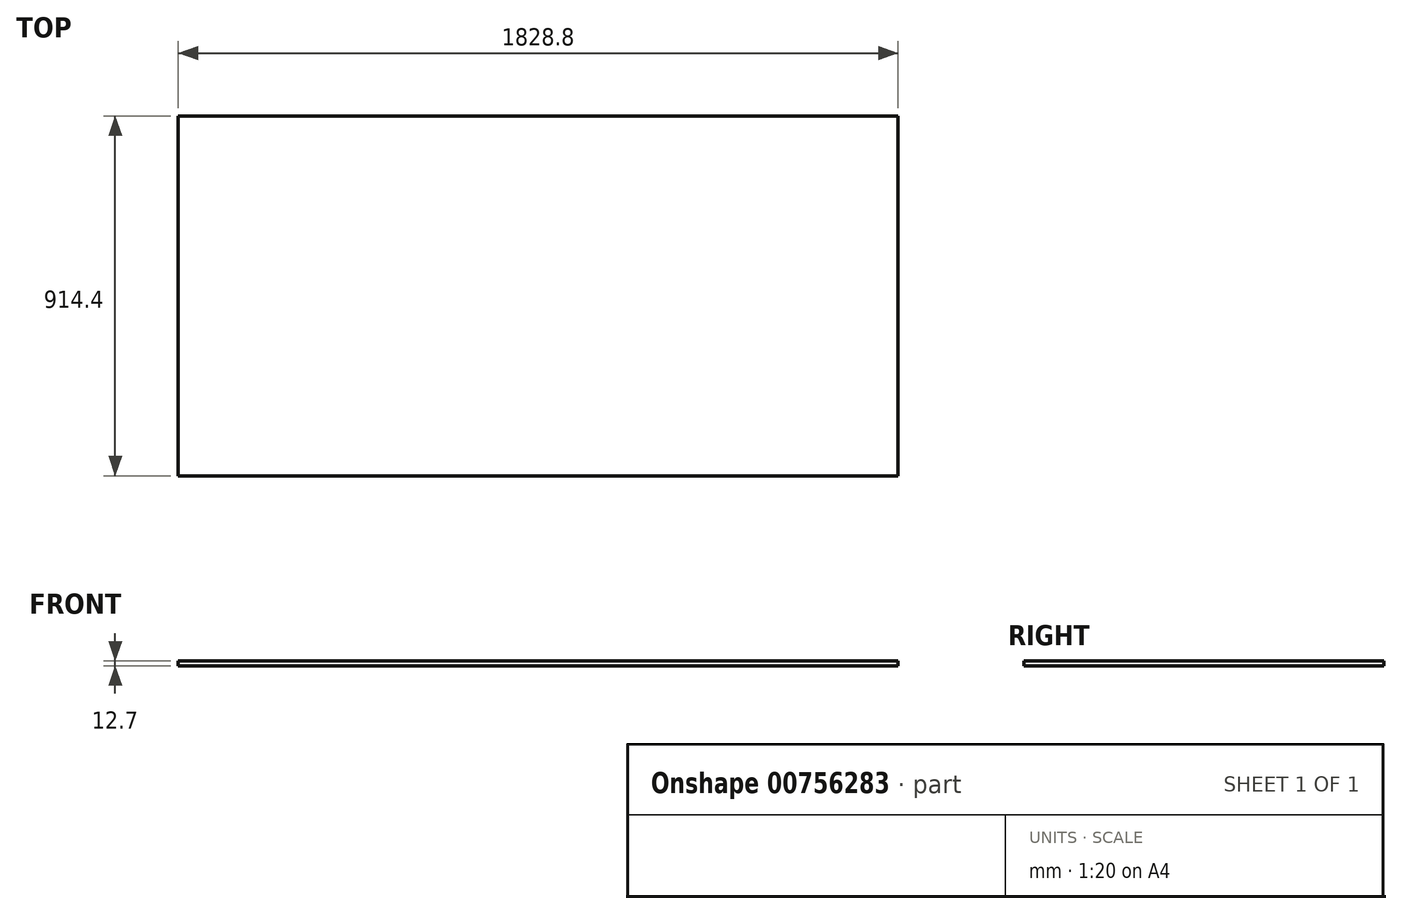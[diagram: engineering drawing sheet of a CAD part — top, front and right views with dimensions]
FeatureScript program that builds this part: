
annotation { "Feature Type Name" : "Feature", "Feature Type Description" : "" }
export const myFeature = defineFeature(function(context is Context, id is Id, definition is map)
    precondition{}
    {
        {
            var Q0;
            Q0=qCreatedBy(makeId("Top.planeOp"),FACE);
            var sketch = newSketch(context, id + "F0", { "sketchPlane" : qUnion([Q0])});
            skLineSegment(sketch, "E0.bottom", {"start": v(914.4, 457.2) * mm, "end": v(-914.4, 457.2) * mm});
            skLineSegment(sketch, "E0.top", {"start": v(914.4, -457.2) * mm, "end": v(-914.4, -457.2) * mm});
            skLineSegment(sketch, "E0.left", {"start": v(914.4, 457.2) * mm, "end": v(914.4, -457.2) * mm});
            skLineSegment(sketch, "E0.right", {"start": v(-914.4, 457.2) * mm, "end": v(-914.4, -457.2) * mm});
            skPoint(sketch, "E0.middle", {"position": v(0, 0) * mm});
            skSolve(sketch);
        }
        {
            var Q0;
            Q0=makeQuery(id+"F0.imprint","IMPRINT",FACE,{"disambiguationData":[TD([[makeQuery(id+"F0.imprint","IMPRINT",EDGE,{"derivedFrom":sQuery(id+"F0.wireOp",EDGE,"E0.bottom")}),1.0]])]});
            extrude(context, id + "F1", {"entities" : qUnion([Q0]), "depth" : 12.7 * mm, "offsetDistance" : 25.4 * mm});
        }
    });
